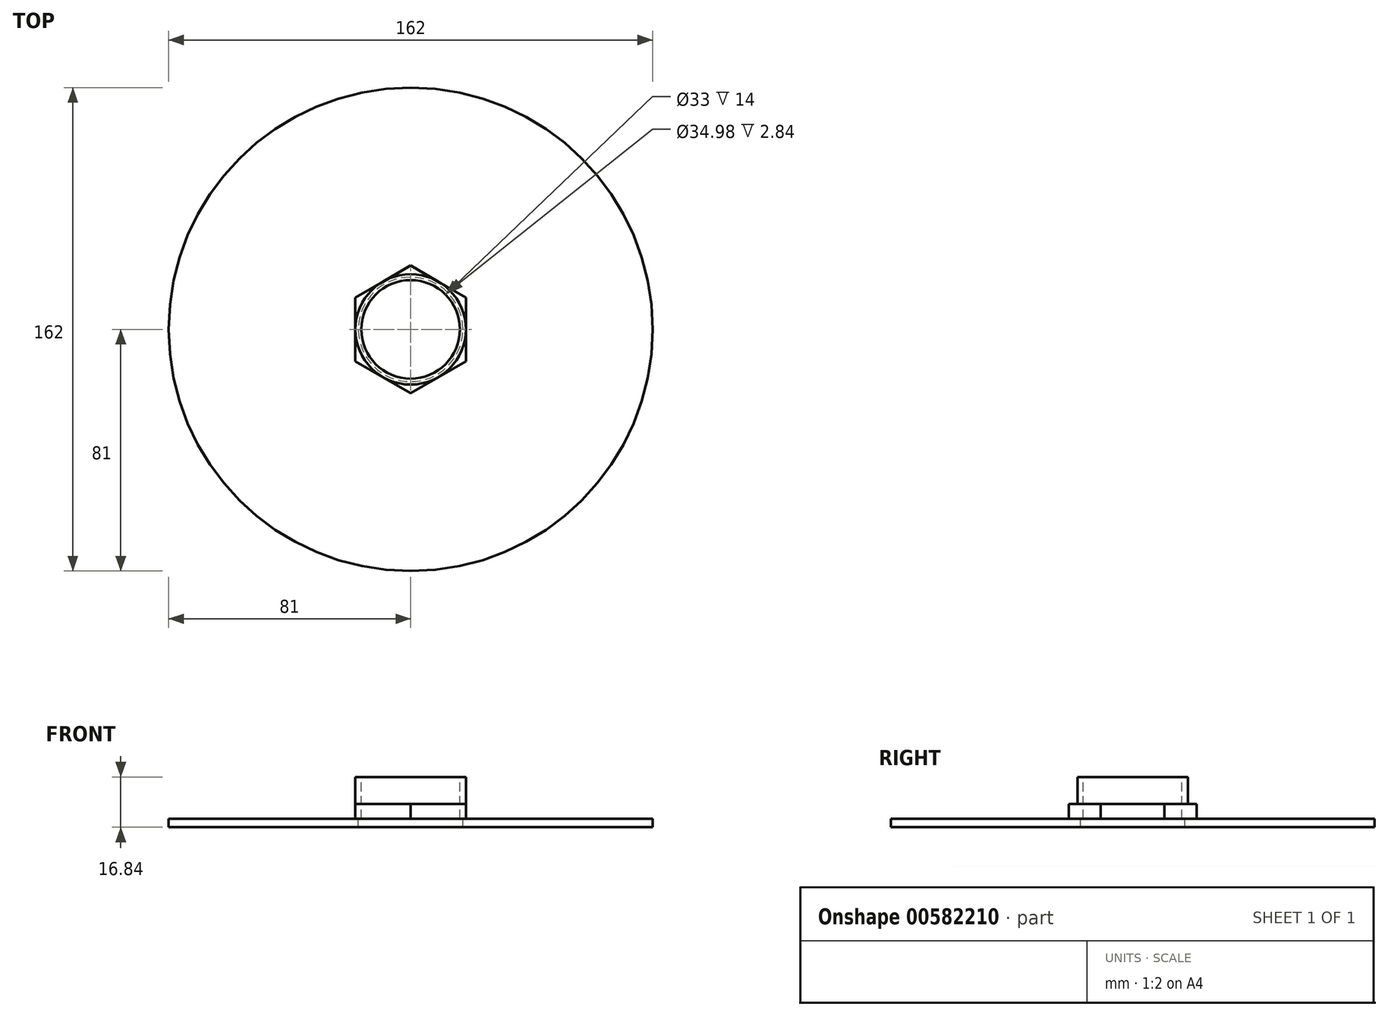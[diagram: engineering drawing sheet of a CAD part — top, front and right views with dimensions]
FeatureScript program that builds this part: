
annotation { "Feature Type Name" : "Feature", "Feature Type Description" : "" }
export const myFeature = defineFeature(function(context is Context, id is Id, definition is map)
    precondition{}
    {
        {
            var Q0;
            Q0=qCreatedBy(makeId("Top.planeOp"),FACE);
            var sketch = newSketch(context, id + "F0", { "sketchPlane" : qUnion([Q0])});
            skCircle(sketch, "E0.cCircle", {"center": v(0, 0) * mm, "radius": 18.5 * mm, "construction": true});
            skLineSegment(sketch, "E0.0", {"start": v(18.5, 10.68) * mm, "end": v(18.5, -10.68) * mm});
            skLineSegment(sketch, "E0.1", {"start": v(18.5, -10.68) * mm, "end": v(0, -21.36) * mm});
            skLineSegment(sketch, "E0.2", {"start": v(0, -21.36) * mm, "end": v(-18.5, -10.68) * mm});
            skLineSegment(sketch, "E0.3", {"start": v(-18.5, -10.68) * mm, "end": v(-18.5, 10.68) * mm});
            skLineSegment(sketch, "E0.4", {"start": v(-18.5, 10.68) * mm, "end": v(0, 21.36) * mm});
            skLineSegment(sketch, "E0.5", {"start": v(0, 21.36) * mm, "end": v(18.5, 10.68) * mm});
            skPoint(sketch, "E0.0.midPoint", {"position": v(18.5, 0) * mm});
            skCircle(sketch, "E1", {"center": v(0, 0) * mm, "radius": 18.5 * mm});
            skSolve(sketch);
        }
        {
            var Q0;
            Q0 = qSketchRegion(id + "F0", true);
            extrude(context, id + "F1", {"entities" : qUnion([Q0]), "depth" : 5 * mm, "offsetDistance" : 25 * mm});
        }
        {
            var Q0;
            Q0=makeQuery(id+"F1.opExtrude","CAP_FACE",FACE,{"disambiguationData":[OSD([sQuery(id+"F0.wireOp",EDGE,"E0.0"),sQuery(id+"F0.wireOp",EDGE,"E0.1"),sQuery(id+"F0.wireOp",EDGE,"E0.2"),sQuery(id+"F0.wireOp",EDGE,"E0.3"),sQuery(id+"F0.wireOp",EDGE,"E0.4"),sQuery(id+"F0.wireOp",EDGE,"E0.5")])],"isStart":false});
            var sketch = newSketch(context, id + "F2", { "sketchPlane" : qUnion([Q0])});
            skCircle(sketch, "E2", {"center": v(0, 0) * mm, "radius": 18.5 * mm});
            skSolve(sketch);
        }
        {
            var Q0;
            Q0 = qSketchRegion(id + "F2", true);
            extrude(context, id + "F3", {"entities" : qUnion([Q0]), "operationType" : NewBodyOperationType.ADD, "depth" : 9 * mm, "offsetDistance" : 25 * mm});
        }
        {
            var Q0;
            Q0=makeQuery(id+"F3.opExtrude","CAP_FACE",FACE,{"disambiguationData":[OSD([sQuery(id+"F2.wireOp",EDGE,"E2")])],"isStart":false});
            var sketch = newSketch(context, id + "F4", { "sketchPlane" : qUnion([Q0])});
            skCircle(sketch, "E3", {"center": v(0, 0) * mm, "radius": 16.5 * mm});
            skSolve(sketch);
        }
        {
            var Q0;
            Q0=makeQuery(id+"F4.imprint","IMPRINT",FACE,{"disambiguationData":[TD([[makeQuery(id+"F4.imprint","IMPRINT",EDGE,{"derivedFrom":sQuery(id+"F4.wireOp",EDGE,"E3")}),1.0]])]});
            var Q1;
            Q1=sQuery(id+"F4.wireOp",EDGE,"E3");
            extrude(context, id + "F5", {"entities" : qUnion([Q0]), "operationType" : NewBodyOperationType.REMOVE, "surfaceEntities" : qUnion([Q1]), "oppositeDirection" : true, "depth" : 25 * mm, "offsetDistance" : 25 * mm});
        }
        {
            var Q0;
            Q0=qCreatedBy(makeId("Top.planeOp"),FACE);
            var sketch = newSketch(context, id + "F6", { "sketchPlane" : qUnion([Q0])});
            skCircle(sketch, "E4", {"center": v(0, 0) * mm, "radius": 81 * mm});
            skSolve(sketch);
        }
        {
            var Q0;
            Q0=makeQuery(id+"F6.imprint","IMPRINT",FACE,{"disambiguationData":[TD([[makeQuery(id+"F6.imprint","IMPRINT",EDGE,{"derivedFrom":sQuery(id+"F6.wireOp",EDGE,"E4")}),1.0]])]});
            extrude(context, id + "F7", {"entities" : qUnion([Q0]), "operationType" : NewBodyOperationType.ADD, "oppositeDirection" : true, "depth" : 2.84 * mm, "offsetDistance" : 25 * mm});
        }
        {
            var Q0;
            Q0=makeQuery(id+"F6.imprint","IMPRINT",FACE,{"disambiguationData":[TD([[makeQuery(id+"F6.imprint","IMPRINT",EDGE,{"derivedFrom":sQuery(id+"F6.wireOp",EDGE,"E4")}),1.0]])]});
            var sketch = newSketch(context, id + "F8", { "sketchPlane" : qUnion([Q0])});
            skCircle(sketch, "E5", {"center": v(0, 0) * mm, "radius": 17.49 * mm});
            skSolve(sketch);
        }
        {
            var Q0;
            Q0 = qSketchRegion(id + "F8", true);
            extrude(context, id + "F9", {"entities" : qUnion([Q0]), "operationType" : NewBodyOperationType.REMOVE, "oppositeDirection" : true, "depth" : 25 * mm, "offsetDistance" : 25 * mm});
        }
    });
